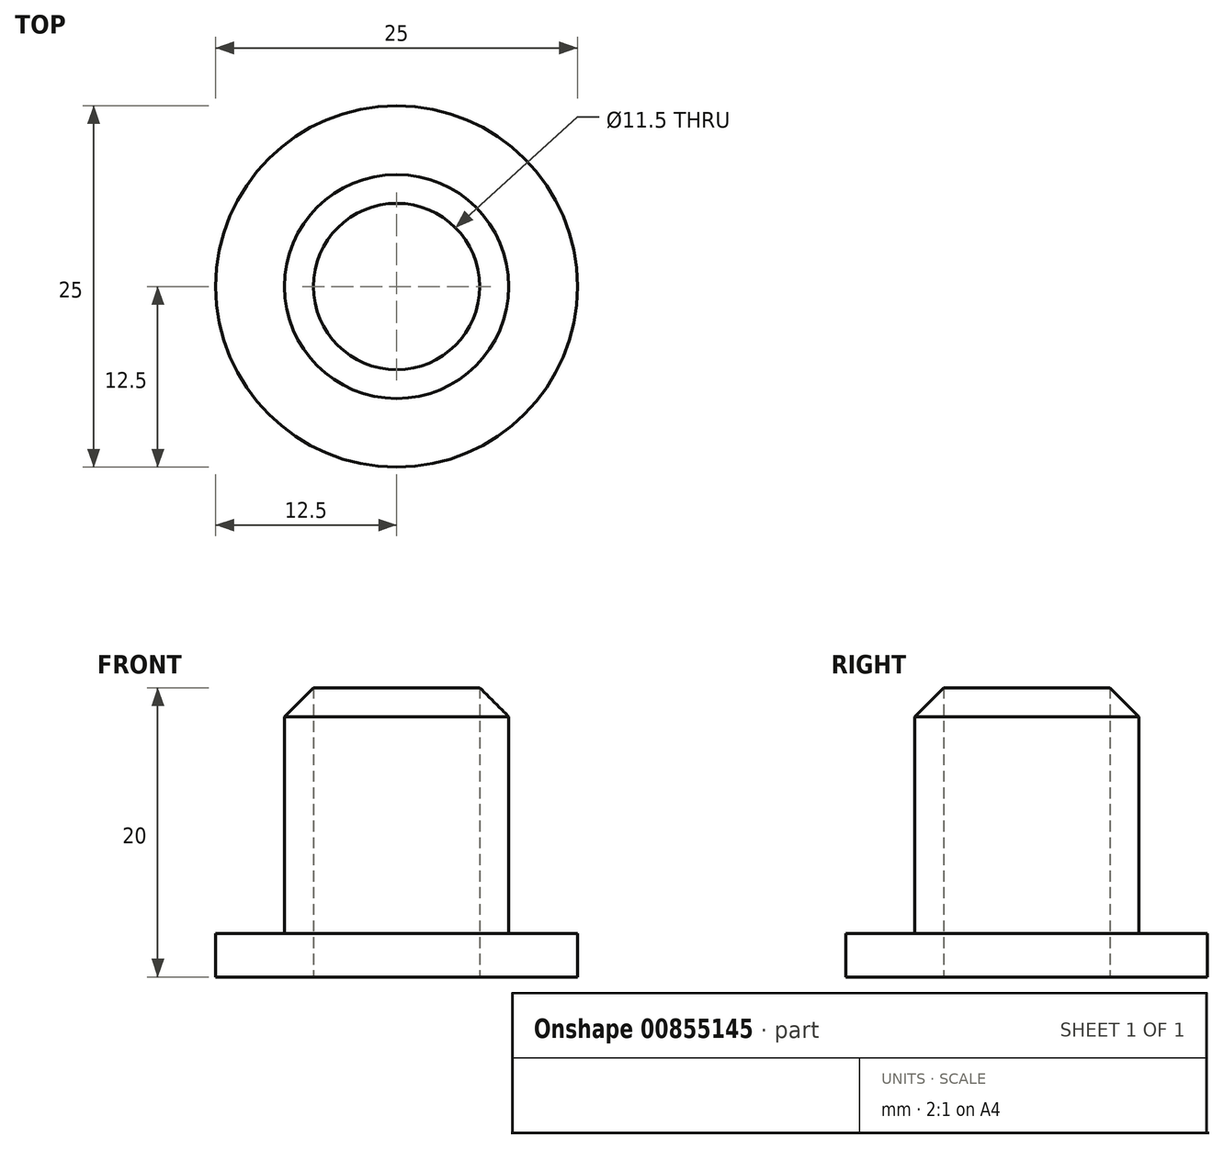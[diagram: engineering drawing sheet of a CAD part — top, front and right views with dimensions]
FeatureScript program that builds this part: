
annotation { "Feature Type Name" : "Feature", "Feature Type Description" : "" }
export const myFeature = defineFeature(function(context is Context, id is Id, definition is map)
    precondition{}
    {
        {
            var Q0;
            Q0=qCreatedBy(makeId("Top.planeOp"),FACE);
            var sketch = newSketch(context, id + "F0", { "sketchPlane" : qUnion([Q0])});
            skCircle(sketch, "E0", {"center": v(0, 0) * mm, "radius": 5.75 * mm});
            skCircle(sketch, "E1", {"center": v(0, 0) * mm, "radius": 7.75 * mm});
            skSolve(sketch);
        }
        {
            var Q0;
            Q0=makeQuery(id+"F0.imprint","IMPRINT",FACE,{"disambiguationData":[TD([[makeQuery(id+"F0.imprint","IMPRINT",EDGE,{"derivedFrom":sQuery(id+"F0.wireOp",EDGE,"E0")}),-1.0]])]});
            extrude(context, id + "F1", {"entities" : qUnion([Q0]), "depth" : 20 * mm, "offsetDistance" : 25 * mm});
        }
        {
            var Q0;
            Q0=qCreatedBy(makeId("Top.planeOp"),FACE);
            var sketch = newSketch(context, id + "F2", { "sketchPlane" : qUnion([Q0])});
            skCircle(sketch, "E2", {"center": v(0, 0) * mm, "radius": 12.5 * mm});
            skCircle(sketch, "E3.0", {"center": v(0, 0) * mm, "radius": 7.75 * mm});
            skSolve(sketch);
        }
        {
            var Q0;
            Q0=makeQuery(id+"F2.imprint","IMPRINT",FACE,{"disambiguationData":[TD([[makeQuery(id+"F2.imprint","IMPRINT",EDGE,{"derivedFrom":sQuery(id+"F2.wireOp",EDGE,"E2")}),1.0]])]});
            extrude(context, id + "F3", {"entities" : qUnion([Q0]), "operationType" : NewBodyOperationType.ADD, "depth" : 3 * mm, "offsetDistance" : 25 * mm});
        }
        {
            var Q0;
            Q0=makeQuery(id+"F1.opExtrude","CAP_EDGE",EDGE,{"disambiguationData":[OSD([sQuery(id+"F0.wireOp",EDGE,"E1")])],"isStart":false});
            chamfer(context, id + "F4", {"entities" : qUnion([Q0]), "width" : 2 * mm, "tangentPropagation" : true});
        }
    });
